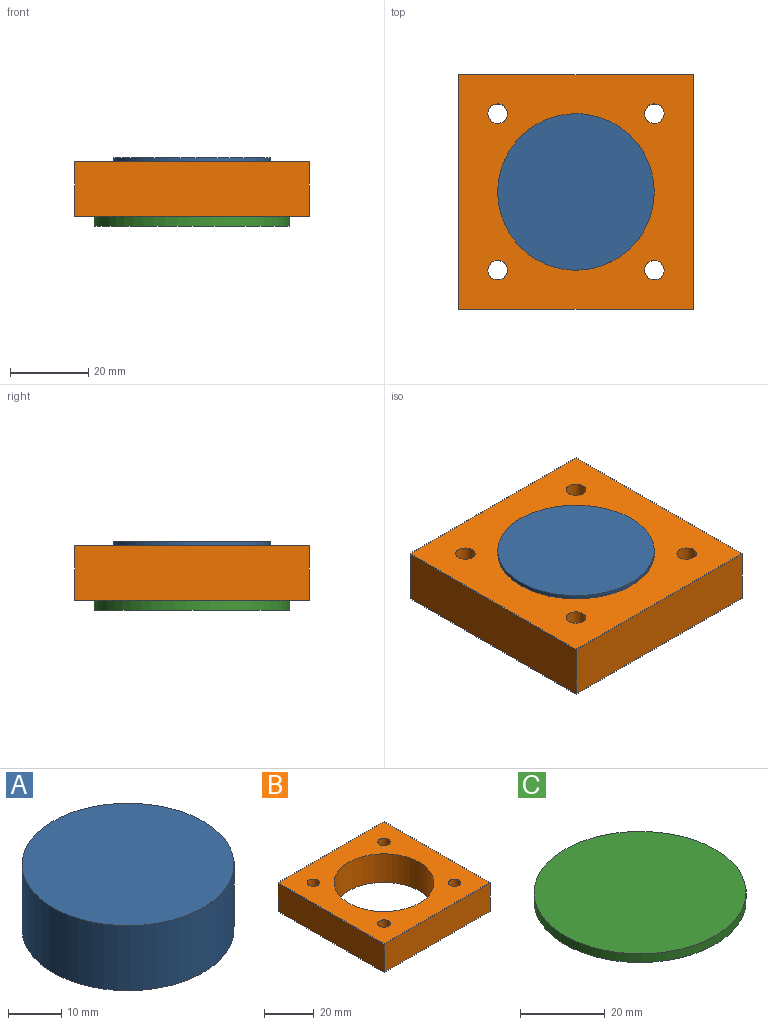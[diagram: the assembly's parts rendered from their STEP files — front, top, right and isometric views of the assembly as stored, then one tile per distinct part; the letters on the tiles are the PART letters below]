
ASSEMBLY  parts=3 mates=2
PART A: 3 faces, bbox 40x40x15 mm
  f0: cylinder r=20mm len=40mm, axis (0,0,-1), area 1885mm2, adj f1,f2
  f1: plane 40x40mm, normal (0,0,1), area 1256.6mm2, adj f0
  f2: plane 40x40mm, normal (0,0,-1), area 1256.6mm2, adj f0
PART B: 11 faces, bbox 60x60x14 mm
  f0: plane 60x14mm, normal (-1,0,0), area 840mm2, adj f1,f3,f9,f10
  f1: plane 60x14mm, normal (0,-1,0), area 840mm2, adj f0,f2,f9,f10
  f2: plane 60x14mm, normal (1,0,0), area 840mm2, adj f1,f3,f9,f10
  f3: plane 60x14mm, normal (0,1,0), area 840mm2, adj f0,f2,f9,f10
  f4: cylinder r=20mm len=40mm, axis (0,0,-1), area 1759.3mm2, adj f9,f10
  f5: cylinder r=2.5mm len=14mm, axis (0,0,-1), area 219.9mm2, adj f9,f10
  f6: cylinder r=2.5mm len=14mm, axis (0,0,-1), area 219.9mm2, adj f9,f10
  f7: cylinder r=2.5mm len=14mm, axis (0,0,-1), area 219.9mm2, adj f9,f10
  f8: cylinder r=2.5mm len=14mm, axis (0,0,-1), area 219.9mm2, adj f9,f10
  f9: plane 60x60mm, normal (0,0,1), area 2264.8mm2, adj f0,f1,f2,f3,f4,f5,f6,f7
  f10: plane 60x60mm, normal (0,0,-1), area 2264.8mm2, adj f0,f1,f2,f3,f4,f5,f6,f7
PART C: 3 faces, bbox 50x50x2.5 mm
  f0: cylinder r=25mm len=50mm, axis (0,0,-1), area 392.7mm2, adj f1,f2
  f1: plane 50x50mm, normal (0,0,1), area 1963.5mm2, adj f0
  f2: plane 50x50mm, normal (0,0,-1), area 1963.5mm2, adj f0
PLACE A t=(91.96,0,2.5)mm
PLACE B t=(91.96,-55.02,2.5)mm
PLACE C at identity
MATE fastened A.f0 <-> C.f0  axis (0,0,-1) through (91.96,0,2.5)mm
MATE revolute B.f4 <-> A.f0  axis (0,0,-1) through (91.96,0,2.5)mm
